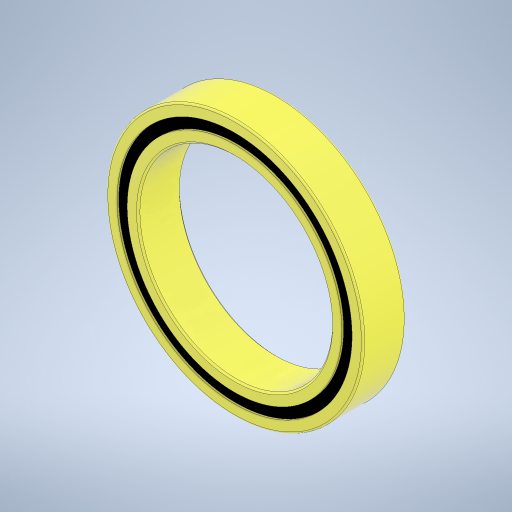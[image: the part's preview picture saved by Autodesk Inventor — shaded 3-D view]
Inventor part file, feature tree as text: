
AUTODESK INVENTOR PART (.ipt)
format: ipt  version: 2024 (Build 280153000, 153)  size: 320,000 bytes
history: native  units: in
note: dims shown in document units (in); Inventor stores cm internally (conversion verified against a paired STEP export)
features: extrude x2, sketch x2, fillet x1, chamfer x1, direct_edit x1, other x1
ambient origin geometry x8: Origin, YZ Plane, XZ Plane, XY Plane, X Axis, Y Axis, Z Axis, Center Point
bodies: Solid1 (feature_tree)
feature tree (8):
  extrude  "Extrusion1"  Depth=0.75in
  fillet  "Fillet1"  Radius=0.032in
  chamfer  "Chamfer1"  Distance=0.125in
  extrude  "Extrusion2"  Depth=0.3937in
  direct_edit  "Direct Edit1"
  sketch  "Sketch1"  dims[d0=0.5625in d1=0.75in d2=0.032in]
  sketch  "Sketch2"  dims[d3=0.032in d4=0.125in d5=0.0in d6=0.005in d7=0.005in d8=0.125in d9=45.0deg d10=0.115in d11=0.0in d12=3.937in d13=0.3937in d14=0.3937in]
  other  "Scale1"
